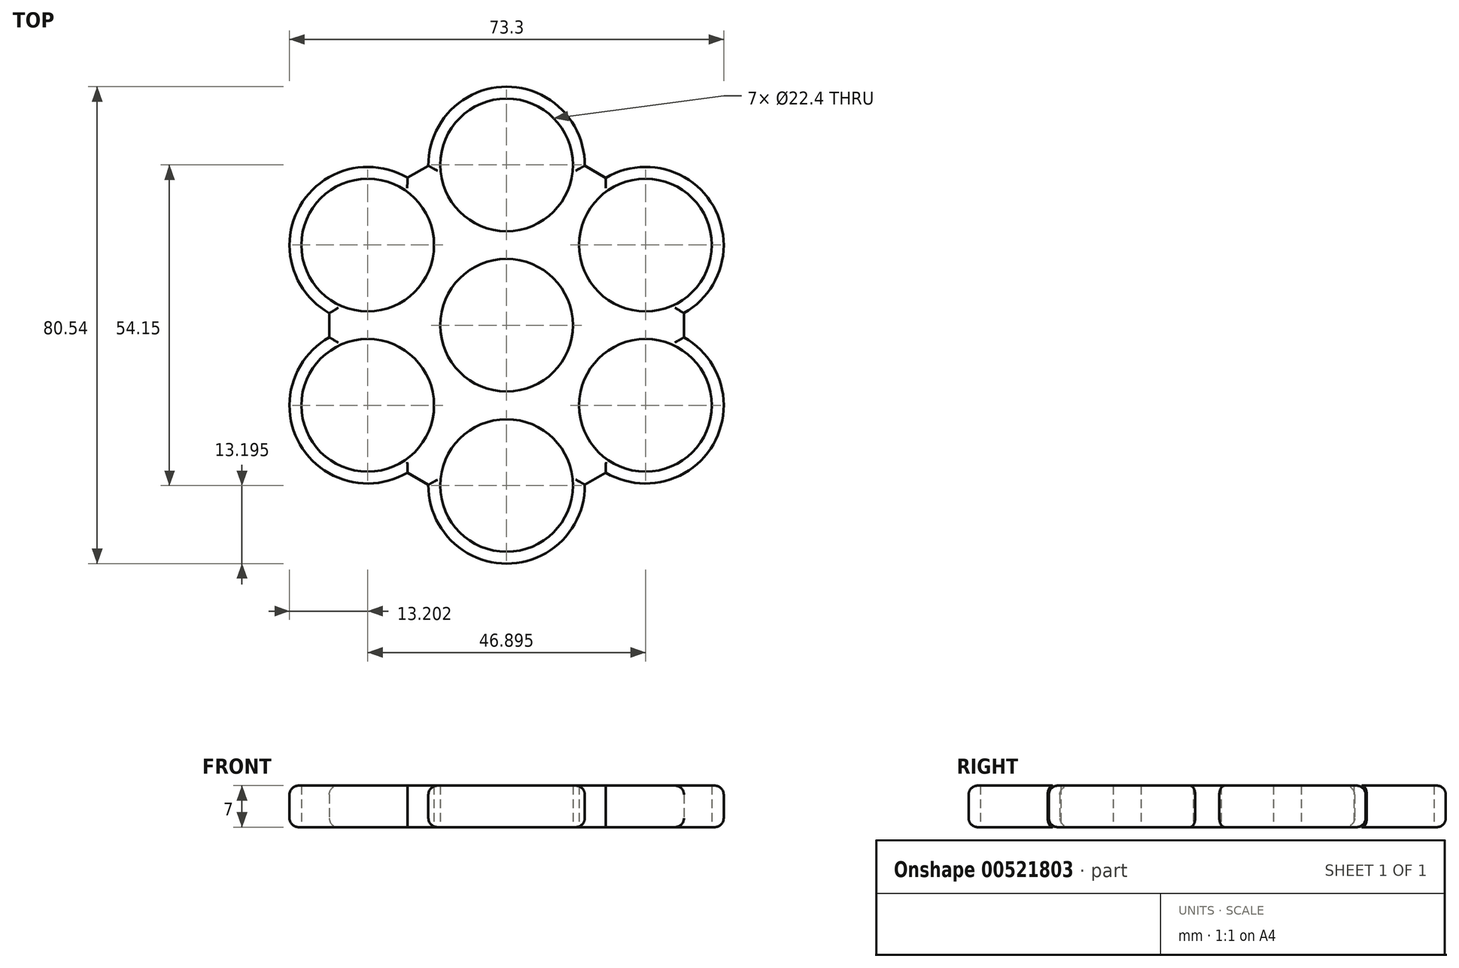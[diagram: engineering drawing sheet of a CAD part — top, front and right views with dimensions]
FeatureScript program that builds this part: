
annotation { "Feature Type Name" : "Feature", "Feature Type Description" : "" }
export const myFeature = defineFeature(function(context is Context, id is Id, definition is map)
    precondition{}
    {
        {
            var Q0;
            Q0=qCreatedBy(makeId("Top.planeOp"),FACE);
            var sketch = newSketch(context, id + "F0", { "sketchPlane" : qUnion([Q0])});
            skCircle(sketch, "E0", {"center": v(0, 0) * mm, "radius": 11.2 * mm});
            skCircle(sketch, "E1", {"center": v(0, 27.07) * mm, "radius": 11.2 * mm});
            skArc(sketch, "E2", {"start": v(13.2, 26.95) * mm, "mid": v(0, 40.27) * mm, "end": v(-13.2, 26.93) * mm});
            skArc(sketch, "E3.1.0", {"start": v(-16.74, 24.9) * mm, "mid": v(-34.88, 20.13) * mm, "end": v(-29.92, 2.04) * mm});
            skCircle(sketch, "E3.1.1", {"center": v(-23.45, 13.54) * mm, "radius": 11.2 * mm});
            skArc(sketch, "E3.2.0", {"start": v(-29.94, -2.04) * mm, "mid": v(-34.88, -20.14) * mm, "end": v(-16.73, -24.9) * mm});
            skCircle(sketch, "E3.2.1", {"center": v(-23.45, -13.54) * mm, "radius": 11.2 * mm});
            skArc(sketch, "E4.1.3.0", {"start": v(-13.2, -26.95) * mm, "mid": v(0, -40.27) * mm, "end": v(13.2, -26.93) * mm});
            skCircle(sketch, "E4.2.3.0", {"center": v(0, -27.07) * mm, "radius": 11.2 * mm});
            skArc(sketch, "E4.1.4.0", {"start": v(16.74, -24.9) * mm, "mid": v(34.88, -20.13) * mm, "end": v(29.92, -2.04) * mm});
            skCircle(sketch, "E4.2.4.0", {"center": v(23.45, -13.54) * mm, "radius": 11.2 * mm});
            skArc(sketch, "E4.1.5.0", {"start": v(29.94, 2.04) * mm, "mid": v(34.88, 20.14) * mm, "end": v(16.73, 24.9) * mm});
            skCircle(sketch, "E4.2.5.0", {"center": v(23.45, 13.54) * mm, "radius": 11.2 * mm});
            skLineSegment(sketch, "E5", {"start": v(13.2, 26.95) * mm, "end": v(16.73, 24.9) * mm});
            skLineSegment(sketch, "E6", {"start": v(29.94, 2.04) * mm, "end": v(29.92, -2.04) * mm});
            skLineSegment(sketch, "E7", {"start": v(16.74, -24.9) * mm, "end": v(13.2, -26.93) * mm});
            skLineSegment(sketch, "E8", {"start": v(-13.2, -26.95) * mm, "end": v(-16.73, -24.9) * mm});
            skLineSegment(sketch, "E9", {"start": v(-29.94, -2.04) * mm, "end": v(-29.92, 2.04) * mm});
            skLineSegment(sketch, "E10", {"start": v(-16.74, 24.9) * mm, "end": v(-13.2, 26.93) * mm});
            skPoint(sketch, "E11.start.orphan", {"position": v(-13.47, 7.6) * mm});
            skPoint(sketch, "E12.start.orphan", {"position": v(-14.26, -7.13) * mm});
            skPoint(sketch, "E13.start.orphan", {"position": v(0, -15.42) * mm});
            skPoint(sketch, "E14.start.orphan", {"position": v(13.95, -7.13) * mm});
            skPoint(sketch, "E15.start.orphan", {"position": v(13.95, 7.6) * mm});
            skSolve(sketch);
        }
        {
            var Q0;
            Q0=makeQuery(id+"F0.imprint","IMPRINT",FACE,{"disambiguationData":[TD([[makeQuery(id+"F0.imprint","IMPRINT",EDGE,{"derivedFrom":sQuery(id+"F0.wireOp",EDGE,"E0")}),-1.0]])]});
            extrude(context, id + "F1", {"entities" : qUnion([Q0]), "depth" : 7 * mm, "offsetDistance" : 25 * mm});
        }
        {
            var Q0;
            Q0=makeQuery(id+"F1.opExtrude","CAP_EDGE",EDGE,{"disambiguationData":[OSD([sQuery(id+"F0.wireOp",EDGE,"E2")])],"isStart":true});
            var Q1;
            Q1=makeQuery(id+"F1.opExtrude","CAP_EDGE",EDGE,{"disambiguationData":[OSD([sQuery(id+"F0.wireOp",EDGE,"E10")])],"isStart":true});
            var Q2;
            Q2=makeQuery(id+"F1.opExtrude","CAP_EDGE",EDGE,{"disambiguationData":[OSD([sQuery(id+"F0.wireOp",EDGE,"E3.1.0")])],"isStart":true});
            var Q3;
            Q3=makeQuery(id+"F1.opExtrude","CAP_EDGE",EDGE,{"disambiguationData":[OSD([sQuery(id+"F0.wireOp",EDGE,"E9")])],"isStart":true});
            var Q4;
            Q4=makeQuery(id+"F1.opExtrude","CAP_EDGE",EDGE,{"disambiguationData":[OSD([sQuery(id+"F0.wireOp",EDGE,"E3.2.0")])],"isStart":true});
            var Q5;
            Q5=makeQuery(id+"F1.opExtrude","CAP_EDGE",EDGE,{"disambiguationData":[OSD([sQuery(id+"F0.wireOp",EDGE,"E8")])],"isStart":true});
            var Q6;
            Q6=makeQuery(id+"F1.opExtrude","CAP_EDGE",EDGE,{"disambiguationData":[OSD([sQuery(id+"F0.wireOp",EDGE,"E4.1.3.0")])],"isStart":true});
            var Q7;
            Q7=makeQuery(id+"F1.opExtrude","CAP_EDGE",EDGE,{"disambiguationData":[OSD([sQuery(id+"F0.wireOp",EDGE,"E7")])],"isStart":true});
            var Q8;
            Q8=makeQuery(id+"F1.opExtrude","CAP_EDGE",EDGE,{"disambiguationData":[OSD([sQuery(id+"F0.wireOp",EDGE,"E4.1.4.0")])],"isStart":true});
            var Q9;
            Q9=makeQuery(id+"F1.opExtrude","CAP_EDGE",EDGE,{"disambiguationData":[OSD([sQuery(id+"F0.wireOp",EDGE,"E4.1.5.0")])],"isStart":true});
            var Q10;
            Q10=makeQuery(id+"F1.opExtrude","CAP_EDGE",EDGE,{"disambiguationData":[OSD([sQuery(id+"F0.wireOp",EDGE,"E5")])],"isStart":true});
            var Q11;
            Q11=makeQuery(id+"F1.opExtrude","CAP_EDGE",EDGE,{"disambiguationData":[OSD([sQuery(id+"F0.wireOp",EDGE,"E6")])],"isStart":true});
            var Q12;
            Q12=makeQuery(id+"F1.opExtrude","CAP_EDGE",EDGE,{"disambiguationData":[OSD([sQuery(id+"F0.wireOp",EDGE,"E10")])],"isStart":false});
            var Q13;
            Q13=makeQuery(id+"F1.opExtrude","CAP_EDGE",EDGE,{"disambiguationData":[OSD([sQuery(id+"F0.wireOp",EDGE,"E2")])],"isStart":false});
            var Q14;
            Q14=makeQuery(id+"F1.opExtrude","CAP_EDGE",EDGE,{"disambiguationData":[OSD([sQuery(id+"F0.wireOp",EDGE,"E5")])],"isStart":false});
            var Q15;
            Q15=makeQuery(id+"F1.opExtrude","CAP_EDGE",EDGE,{"disambiguationData":[OSD([sQuery(id+"F0.wireOp",EDGE,"E4.1.5.0")])],"isStart":false});
            var Q16;
            Q16=makeQuery(id+"F1.opExtrude","CAP_EDGE",EDGE,{"disambiguationData":[OSD([sQuery(id+"F0.wireOp",EDGE,"E6")])],"isStart":false});
            var Q17;
            Q17=makeQuery(id+"F1.opExtrude","CAP_EDGE",EDGE,{"disambiguationData":[OSD([sQuery(id+"F0.wireOp",EDGE,"E4.1.4.0")])],"isStart":false});
            var Q18;
            Q18=makeQuery(id+"F1.opExtrude","CAP_EDGE",EDGE,{"disambiguationData":[OSD([sQuery(id+"F0.wireOp",EDGE,"E7")])],"isStart":false});
            var Q19;
            Q19=makeQuery(id+"F1.opExtrude","CAP_EDGE",EDGE,{"disambiguationData":[OSD([sQuery(id+"F0.wireOp",EDGE,"E4.1.3.0")])],"isStart":false});
            var Q20;
            Q20=makeQuery(id+"F1.opExtrude","CAP_EDGE",EDGE,{"disambiguationData":[OSD([sQuery(id+"F0.wireOp",EDGE,"E8")])],"isStart":false});
            var Q21;
            Q21=makeQuery(id+"F1.opExtrude","CAP_EDGE",EDGE,{"disambiguationData":[OSD([sQuery(id+"F0.wireOp",EDGE,"E3.2.0")])],"isStart":false});
            var Q22;
            Q22=makeQuery(id+"F1.opExtrude","CAP_EDGE",EDGE,{"disambiguationData":[OSD([sQuery(id+"F0.wireOp",EDGE,"E9")])],"isStart":false});
            var Q23;
            Q23=makeQuery(id+"F1.opExtrude","CAP_EDGE",EDGE,{"disambiguationData":[OSD([sQuery(id+"F0.wireOp",EDGE,"E3.1.0")])],"isStart":false});
            fillet(context, id + "F2", {"entities" : qUnion([Q0, Q1, Q2, Q3, Q4, Q5, Q6, Q7, Q8, Q9, Q10, Q11, Q12, Q13, Q14, Q15, Q16, Q17, Q18, Q19, Q20, Q21, Q22, Q23]), "radius" : 1.5 * mm, "tangentPropagation" : true, "allowEdgeOverflow" : false});
        }
    });
